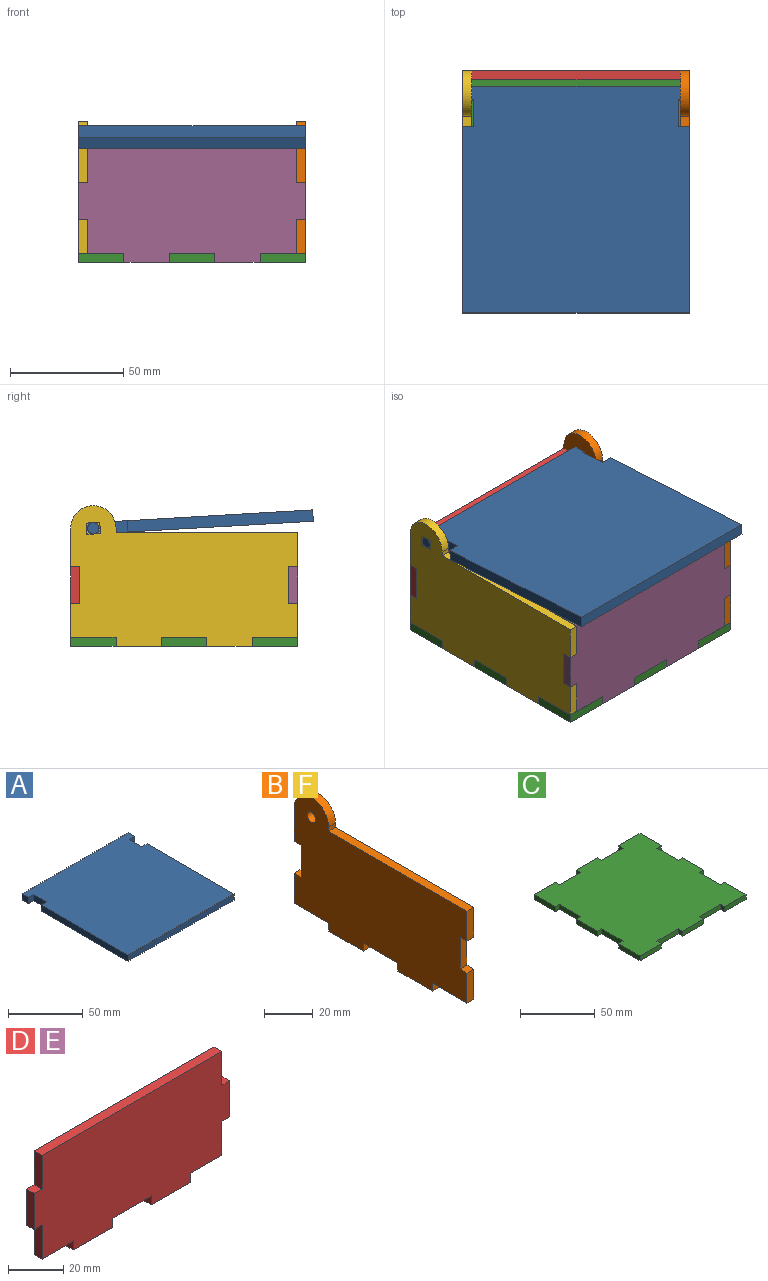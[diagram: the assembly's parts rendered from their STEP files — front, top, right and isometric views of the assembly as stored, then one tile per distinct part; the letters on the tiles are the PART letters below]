
ASSEMBLY  parts=6 mates=5
PART A: 14 faces, bbox 100x100x5 mm
  f0: plane 82x5mm, normal (1,0,0), area 410mm2, adj f1,f11,f12,f13
  f1: plane 5x5mm, normal (0,1,0), area 25mm2, adj f0,f2,f12,f13
  f2: plane 12x5mm, normal (1,0,0), area 60mm2, adj f1,f3,f12,f13
  f3: plane 5x5mm, normal (0,-1,0), area 25mm2, adj f2,f4,f12,f13
  f4: plane 6x5mm, normal (1,0,0), area 30mm2, adj f3,f5,f12,f13
  f5: plane 100x5mm, normal (0,1,0), area 500mm2, adj f4,f6,f12,f13
  f6: plane 6x5mm, normal (-1,0,0), area 30mm2, adj f5,f7,f12,f13
  f7: plane 5x5mm, normal (0,-1,0), area 25mm2, adj f6,f8,f12,f13
  f8: plane 12x5mm, normal (-1,0,0), area 60mm2, adj f7,f9,f12,f13
  f9: plane 5x5mm, normal (0,1,0), area 25mm2, adj f8,f10,f12,f13
  f10: plane 82x5mm, normal (-1,0,0), area 410mm2, adj f9,f11,f12,f13
  f11: plane 100x5mm, normal (0,-1,0), area 500mm2, adj f0,f10,f12,f13
  f12: plane 100x100mm, normal (0,0,1), area 9880mm2, adj f0,f1,f2,f3,f4,f5,f6,f7
  f13: plane 100x100mm, normal (0,0,-1), area 9880mm2, adj f0,f1,f2,f3,f4,f5,f6,f7
PART B: 25 faces, bbox 4x100x62 mm
  f0: plane 20x4mm, normal (0,0,-1), area 80mm2, adj f2,f3,f20,f23
  f1: plane 20x4mm, normal (0,0,-1), area 80mm2, adj f2,f3,f18,f21
  f2: plane 100x62mm, normal (1,0,0), area 4809.4mm2, adj f0,f1,f4,f5,f6,f7,f8,f9
  f3: plane 100x62mm, normal (-1,0,0), area 4809.4mm2, adj f0,f1,f4,f5,f6,f7,f8,f9
  f4: plane 4x4mm, normal (0,0,-1), area 16mm2, adj f2,f3,f5,f16
  f5: plane 17x4mm, normal (0,1,0), area 68mm2, adj f2,f3,f4,f6
  f6: cylinder r=10mm len=20mm, axis (-1,0,0), area 125.7mm2, adj f2,f3,f5,f7
  f7: plane 4x2mm, normal (0,-1,0), area 8mm2, adj f2,f3,f6,f8
  f8: plane 80x4mm, normal (0,0,1), area 320mm2, adj f2,f3,f7,f9
  f9: plane 15x4mm, normal (0,-1,0), area 60mm2, adj f2,f3,f8,f10
  f10: plane 4x4mm, normal (0,0,-1), area 16mm2, adj f2,f3,f9,f11
  f11: plane 16x4mm, normal (0,-1,0), area 64mm2, adj f2,f3,f10,f12
  f12: plane 4x4mm, normal (0,0,1), area 16mm2, adj f2,f3,f11,f13
  f13: plane 15x4mm, normal (0,-1,0), area 60mm2, adj f2,f3,f12,f24
  f14: plane 15x4mm, normal (0,1,0), area 60mm2, adj f2,f3,f15,f22
  f15: plane 4x4mm, normal (0,0,1), area 16mm2, adj f2,f3,f14,f16
  f16: plane 16x4mm, normal (0,1,0), area 64mm2, adj f2,f3,f4,f15
  f17: cylinder r=2.5mm len=5mm, axis (-1,0,0), area 62.8mm2, adj f2,f3
  f18: plane 4x4mm, normal (0,-1,0), area 16mm2, adj f1,f2,f3,f19
  f19: plane 20x4mm, normal (0,0,-1), area 80mm2, adj f2,f3,f18,f20
  f20: plane 4x4mm, normal (0,1,0), area 16mm2, adj f0,f2,f3,f19
  f21: plane 4x4mm, normal (0,1,0), area 16mm2, adj f1,f2,f3,f22
  f22: plane 20x4mm, normal (0,0,-1), area 80mm2, adj f2,f3,f14,f21
  f23: plane 4x4mm, normal (0,-1,0), area 16mm2, adj f0,f2,f3,f24
  f24: plane 20x4mm, normal (0,0,-1), area 80mm2, adj f2,f3,f13,f23
PART C: 38 faces, bbox 100x100x4 mm
  f0: plane 20x4mm, normal (0,-1,0), area 80mm2, adj f1,f35,f36,f37
  f1: plane 4x4mm, normal (1,0,0), area 16mm2, adj f0,f2,f36,f37
  f2: plane 20x4mm, normal (0,-1,0), area 80mm2, adj f1,f3,f36,f37
  f3: plane 4x4mm, normal (-1,0,0), area 16mm2, adj f2,f4,f36,f37
  f4: plane 20x4mm, normal (0,-1,0), area 80mm2, adj f3,f5,f36,f37
  f5: plane 4x4mm, normal (1,0,0), area 16mm2, adj f4,f6,f36,f37
  f6: plane 20x4mm, normal (0,-1,0), area 80mm2, adj f5,f7,f36,f37
  f7: plane 4x4mm, normal (-1,0,0), area 16mm2, adj f6,f8,f36,f37
  f8: plane 20x4mm, normal (0,-1,0), area 80mm2, adj f7,f9,f36,f37
  f9: plane 20x4mm, normal (1,0,0), area 80mm2, adj f8,f10,f36,f37
  f10: plane 4x4mm, normal (0,1,0), area 16mm2, adj f9,f11,f36,f37
  f11: plane 20x4mm, normal (1,0,0), area 80mm2, adj f10,f12,f36,f37
  f12: plane 4x4mm, normal (0,-1,0), area 16mm2, adj f11,f13,f36,f37
  f13: plane 20x4mm, normal (1,0,0), area 80mm2, adj f12,f14,f36,f37
  f14: plane 4x4mm, normal (0,1,0), area 16mm2, adj f13,f15,f36,f37
  f15: plane 20x4mm, normal (1,0,0), area 80mm2, adj f14,f16,f36,f37
  f16: plane 4x4mm, normal (0,-1,0), area 16mm2, adj f15,f17,f36,f37
  f17: plane 20x4mm, normal (1,0,0), area 80mm2, adj f16,f18,f36,f37
  f18: plane 20x4mm, normal (0,1,0), area 80mm2, adj f17,f19,f36,f37
  f19: plane 4x4mm, normal (-1,0,0), area 16mm2, adj f18,f20,f36,f37
  f20: plane 20x4mm, normal (0,1,0), area 80mm2, adj f19,f21,f36,f37
  f21: plane 4x4mm, normal (1,0,0), area 16mm2, adj f20,f22,f36,f37
  f22: plane 20x4mm, normal (0,1,0), area 80mm2, adj f21,f23,f36,f37
  f23: plane 4x4mm, normal (-1,0,0), area 16mm2, adj f22,f24,f36,f37
  f24: plane 20x4mm, normal (0,1,0), area 80mm2, adj f23,f25,f36,f37
  f25: plane 4x4mm, normal (1,0,0), area 16mm2, adj f24,f26,f36,f37
  f26: plane 20x4mm, normal (0,1,0), area 80mm2, adj f25,f27,f36,f37
  f27: plane 20x4mm, normal (-1,0,0), area 80mm2, adj f26,f28,f36,f37
  f28: plane 4x4mm, normal (0,-1,0), area 16mm2, adj f27,f29,f36,f37
  f29: plane 20x4mm, normal (-1,0,0), area 80mm2, adj f28,f30,f36,f37
  f30: plane 4x4mm, normal (0,1,0), area 16mm2, adj f29,f31,f36,f37
  f31: plane 20x4mm, normal (-1,0,0), area 80mm2, adj f30,f32,f36,f37
  f32: plane 4x4mm, normal (0,-1,0), area 16mm2, adj f31,f33,f36,f37
  f33: plane 20x4mm, normal (-1,0,0), area 80mm2, adj f32,f34,f36,f37
  f34: plane 4x4mm, normal (0,1,0), area 16mm2, adj f33,f35,f36,f37
  f35: plane 20x4mm, normal (-1,0,0), area 80mm2, adj f0,f34,f36,f37
  f36: plane 100x100mm, normal (0,0,1), area 9360mm2, adj f0,f1,f2,f3,f4,f5,f6,f7
  f37: plane 100x100mm, normal (0,0,-1), area 9360mm2, adj f0,f1,f2,f3,f4,f5,f6,f7
PART D: 22 faces, bbox 100x4x50 mm
  f0: plane 4x4mm, normal (-1,0,0), area 16mm2, adj f1,f19,f20,f21
  f1: plane 20x4mm, normal (0,0,-1), area 80mm2, adj f0,f2,f20,f21
  f2: plane 4x4mm, normal (1,0,0), area 16mm2, adj f1,f3,f20,f21
  f3: plane 16x4mm, normal (0,0,-1), area 64mm2, adj f2,f4,f20,f21
  f4: plane 15x4mm, normal (1,0,0), area 60mm2, adj f3,f5,f20,f21
  f5: plane 4x4mm, normal (0,0,-1), area 16mm2, adj f4,f6,f20,f21
  f6: plane 16x4mm, normal (1,0,0), area 64mm2, adj f5,f7,f20,f21
  f7: plane 4x4mm, normal (0,0,1), area 16mm2, adj f6,f8,f20,f21
  f8: plane 15x4mm, normal (1,0,0), area 60mm2, adj f7,f9,f20,f21
  f9: plane 92x4mm, normal (0,0,1), area 368mm2, adj f8,f10,f20,f21
  f10: plane 15x4mm, normal (-1,0,0), area 60mm2, adj f9,f11,f20,f21
  f11: plane 4x4mm, normal (0,0,1), area 16mm2, adj f10,f12,f20,f21
  f12: plane 16x4mm, normal (-1,0,0), area 64mm2, adj f11,f13,f20,f21
  f13: plane 4x4mm, normal (0,0,-1), area 16mm2, adj f12,f14,f20,f21
  f14: plane 15x4mm, normal (-1,0,0), area 60mm2, adj f13,f15,f20,f21
  f15: plane 16x4mm, normal (0,0,-1), area 64mm2, adj f14,f16,f20,f21
  f16: plane 4x4mm, normal (-1,0,0), area 16mm2, adj f15,f17,f20,f21
  f17: plane 20x4mm, normal (0,0,-1), area 80mm2, adj f16,f18,f20,f21
  f18: plane 4x4mm, normal (1,0,0), area 16mm2, adj f17,f19,f20,f21
  f19: plane 20x4mm, normal (0,0,-1), area 80mm2, adj f0,f18,f20,f21
  f20: plane 100x50mm, normal (0,-1,0), area 4520mm2, adj f0,f1,f2,f3,f4,f5,f6,f7
  f21: plane 100x50mm, normal (0,1,0), area 4520mm2, adj f0,f1,f2,f3,f4,f5,f6,f7
PART E: same geometry as D
PART F: same geometry as B
PLACE A rot(axis=(-1,0,0),3.3deg) t=(-46.11,-39.27,60.46)mm
PLACE B t=(49.89,54.15,10.22)mm
PLACE C t=(-15.66,-27.28,6.18)mm fixed
PLACE D t=(12.36,52.72,-7.34)mm
PLACE E t=(12.36,-43.28,-7.34)mm
PLACE F t=(-46.11,54.15,10.22)mm
MATE fastened E.f20 <-> C.f4  axis (0,-1,0) through (13.89,-47.28,10.18)mm
MATE revolute A.f4 <-> B.f6  axis (1,0,0) through (53.89,42.72,58.18)mm
MATE fastened D.f21 <-> C.f26  axis (0,1,0) through (-26.11,52.72,10.18)mm
MATE fastened F.f3 <-> C.f27  axis (-1,0,0) through (-46.11,32.72,10.18)mm
MATE fastened B.f2 <-> C.f9  axis (1,0,0) through (53.89,-27.28,10.18)mm
